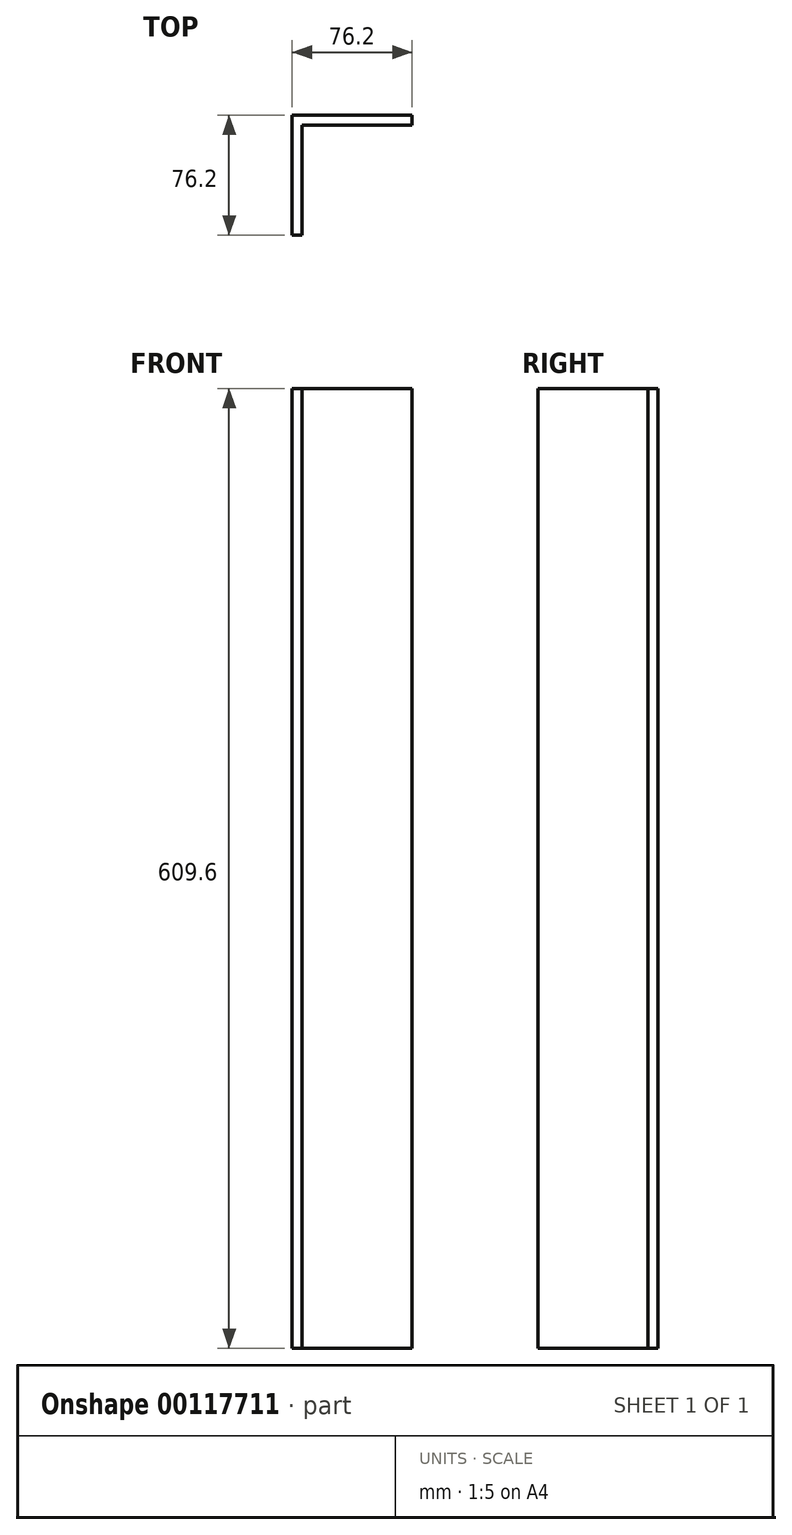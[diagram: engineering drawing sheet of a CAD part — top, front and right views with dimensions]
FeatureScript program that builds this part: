
annotation { "Feature Type Name" : "Feature", "Feature Type Description" : "" }
export const myFeature = defineFeature(function(context is Context, id is Id, definition is map)
    precondition{}
    {
        {
            var Q0;
            Q0=qCreatedBy(makeId("Top.planeOp"),FACE);
            var sketch = newSketch(context, id + "F0", { "sketchPlane" : qUnion([Q0])});
            skLineSegment(sketch, "E0", {"start": v(0, 0) * mm, "end": v(-76.2, 0) * mm});
            skLineSegment(sketch, "E1", {"start": v(-76.2, 0) * mm, "end": v(-76.2, -76.2) * mm});
            skLineSegment(sketch, "E2.0", {"start": v(-69.85, -6.35) * mm, "end": v(-69.85, -76.2) * mm});
            skLineSegment(sketch, "E2.1", {"start": v(0, -6.35) * mm, "end": v(-69.85, -6.35) * mm});
            skLineSegment(sketch, "E3", {"start": v(-76.2, -76.2) * mm, "end": v(-69.85, -76.2) * mm});
            skLineSegment(sketch, "E4", {"start": v(0, 0) * mm, "end": v(0, -6.35) * mm});
            skSolve(sketch);
        }
        {
            var Q0;
            Q0 = qSketchRegion(id + "F0", true);
            extrude(context, id + "F1", {"entities" : qUnion([Q0]), "depth" : 609.6 * mm});
        }
    });
